FCSTD DOCUMENT  (FreeCAD 0.22R36731 (Git))
Label: bridge_suspend
License: All rights reserved
objects: Part::FeaturePython×17, Part::Extrusion×7, Part::Mirroring×6, Sketcher::SketchObject×5, App::Part×3, Part::Sweep×2, Part::Cut×1, Spreadsheet::Sheet×1, Part::MultiFuse×1
note: 39 computed .brp shape members not serialized (recipe doc carries the construction recipe); baked Part::Feature solids carry a one-line shape summary decoded from their .brp

FEATURE [Part::FeaturePython] HShapeSteel  # WARN: FeaturePython — macro-defined, semantics opaque (R4)
  B = 175
  H = 350
  L = 1000
  Placement = pos=(0,500,0) rot=(0,0,-1;1.5708rad)
  Solid = false
  g0 = 7.85
  mass = 0
  size = 11
  standard = SS_Thin
  t1 = 7
  t2 = 11
FEATURE [Part::FeaturePython] HShapeSteel001  # WARN: FeaturePython — macro-defined, semantics opaque (R4)
  B = 175
  H = 350
  L = 1000
  Placement = pos=(0,-500,0) rot=(0,0,1;1.5708rad)
  Solid = false
  g0 = 7.85
  mass = 0
  size = 11
  standard = SS_Thin
  t1 = 7
  t2 = 11
FEATURE [Part::Extrusion] Extrude
  Base = -> HShapeSteel
  Dir = (1,2e-16,0)
  DirMode = 2
  FaceMakerClass = Part::FaceMakerBullseye
  LengthFwd = 13500
  LengthRev = 0
  Solid = false
  Symmetric = true
  expr: LengthFwd = <<Spreadsheet_bridge>>.tankDia + 500
FEATURE [Part::Extrusion] Extrude001
  Base = -> HShapeSteel001
  Dir = (-1,2e-16,0)
  DirMode = 2
  FaceMakerClass = Part::FaceMakerBullseye
  LengthFwd = 13500
  LengthRev = 0
  Solid = false
  Symmetric = true
  expr: LengthFwd = <<Spreadsheet_bridge>>.tankDia + 500
FEATURE [Sketcher::SketchObject] Sketch
  FullyConstrained = true
  sketch-geometry (5):
    g0: LineSegment StartX=-1000 StartY=-1000 StartZ=0 EndX=1000 EndY=-1000 EndZ=0
    g1: LineSegment StartX=1000 StartY=-1000 StartZ=0 EndX=1000 EndY=1000 EndZ=0
    g2: LineSegment StartX=1000 StartY=1000 StartZ=0 EndX=-1000 EndY=1000 EndZ=0
    g3: LineSegment StartX=-1000 StartY=1000 StartZ=0 EndX=-1000 EndY=-1000 EndZ=0
    g4: GeomPoint X=0 Y=0 Z=0
  constraints (12):
    c: Coincident(g0,g1)
    c: Coincident(g1,g2)
    c: Coincident(g2,g3)
    c: Coincident(g3,g0)
    c: Horizontal(g0)
    c: Horizontal(g2)
    c: Vertical(g1)
    c: Vertical(g3)
    c: Symmetric(g2,g0,g4)
    c: Coincident(g4,g-1)
    c: DistanceX(g2,g2) = 2000
    c: DistanceY(g3,g3) = 2000
FEATURE [Part::FeaturePython] ChannelSteel  # WARN: FeaturePython — macro-defined, semantics opaque (R4)
  B = 75
  H = 150
  L = 1000
  Placement = pos=(925,0,200) rot=(0,0,1;0rad)
  Solid = false
  g0 = 7.85
  mass = 0
  size = 3
  standard = SS
  t1 = 6.5
  t2 = 10
FEATURE [Part::Sweep] Sweep
  Frenet = true
  Sections = -> [ChannelSteel]
  Solid = true
  Spine = -> Sketch [Edge3,Edge2,Edge1,Edge4]
  Transition = 1
FEATURE [Sketcher::SketchObject] Sketch014
  AttachmentSupport = -> [Extrude]
  FullyConstrained = true
  MapMode = 5
  Placement = pos=(0,0,350) rot=(0,0,1;0rad)
  sketch-geometry (5):
    g0: LineSegment StartX=-410 StartY=-410 StartZ=0 EndX=410 EndY=-410 EndZ=0
    g1: LineSegment StartX=410 StartY=-410 StartZ=0 EndX=410 EndY=410 EndZ=0
    g2: LineSegment StartX=410 StartY=410 StartZ=0 EndX=-410 EndY=410 EndZ=0
    g3: LineSegment StartX=-410 StartY=410 StartZ=0 EndX=-410 EndY=-410 EndZ=0
    g4: GeomPoint X=0 Y=0 Z=0
  constraints (12):
    c: Coincident(g0,g1)
    c: Coincident(g1,g2)
    c: Coincident(g2,g3)
    c: Coincident(g3,g0)
    c: Horizontal(g0)
    c: Horizontal(g2)
    c: Vertical(g1)
    c: Vertical(g3)
    c: Symmetric(g2,g0,g4)
    c: Coincident(g4,g-1)
    c: DistanceY(g1,g1) = 820
    c: DistanceX(g2,g2) = 820
FEATURE [Part::Extrusion] Extrude009
  Base = -> Sketch014
  Dir = (0,0,1)
  DirMode = 2
  FaceMakerClass = Part::FaceMakerBullseye
  LengthFwd = 20
  LengthRev = 0
  Solid = true
  Symmetric = false
FEATURE [Part::FeaturePython] ChannelSteel001  # WARN: FeaturePython — macro-defined, semantics opaque (R4)
  B = 75
  H = 150
  L = 1000
  Placement = pos=(315,0,200) rot=(0,0,1;0rad)
  Solid = false
  g0 = 7.85
  mass = 0
  size = 3
  standard = SS
  t1 = 6.5
  t2 = 10
FEATURE [Part::Extrusion] Extrude010
  Base = -> ChannelSteel001
  Dir = (0,1,0)
  DirMode = 2
  FaceMakerClass = Part::FaceMakerBullseye
  LengthFwd = 825
  LengthRev = 0
  Solid = false
  Symmetric = true
FEATURE [Part::FeaturePython] Clone001  label="Extrude011"  # Draft clone (typed FeaturePython)
  AttacherType = Attacher::AttachEngine3D
  Fuse = false
  Objects = -> [Extrude010]
  Placement = pos=(7065,-6.2e-14,0) rot=(0,0,1;3.14159rad)
  Scale = (1,1,1)
  expr: .Placement.Base.x = <<Spreadsheet_bridge>>.tankDia / 2 + 565
FEATURE [Part::FeaturePython] Clone002  label="Extrude012"  # Draft clone (typed FeaturePython)
  AttacherType = Attacher::AttachEngine3D
  Fuse = false
  Objects = -> [Extrude010]
  Placement = pos=(1250,0,0) rot=(0,0,1;0rad)
  Scale = (1,1,1)
FEATURE [Part::FeaturePython] Array006  # Draft array (typed FeaturePython)
  Angle = 360
  ArrayType = 0
  Axis = (0,0,1)
  Base = -> Clone002
  Center = (0,0,0)
  Count = 5
  Fuse = false
  IntervalAxis = (0,0,0)
  IntervalX = (1000,0,0)
  IntervalY = (0,100,0)
  IntervalZ = (0,0,100)
  NumberCircles = 3
  NumberPolar = 5
  NumberX = 5
  NumberY = 1
  NumberZ = 1
  RadialDistance = 50
  Symmetry = 1
  TangentialDistance = 25
FEATURE [Part::Mirroring] Mirror  label="Array006 (mirrored)"
  Base = (0,1200,0)
  Normal = (1,0,0)
  Source = -> Array006
FEATURE [Part::Mirroring] Mirror001  label="Extrude011 (mirrored)"
  Base = (0,1200,0)
  Normal = (1,0,0)
  Source = -> Clone001
FEATURE [Part::Mirroring] Mirror002  label="Extrude010 (mirrored)"
  Base = (0,1200,0)
  Normal = (1,0,0)
  Source = -> Extrude010
FEATURE [Sketcher::SketchObject] Sketch015
  AttachmentSupport = -> [Extrude009]
  FullyConstrained = true
  MapMode = 5
  Placement = pos=(0,0,370) rot=(0,0,1;0rad)
  sketch-geometry (1):
    g0: Circle CenterX=0 CenterY=0 CenterZ=0 NormalX=0 NormalY=0 NormalZ=1 AngleXU=0 Radius=150
  constraints (2):
    c: Coincident(g0,g-1)
    c: Diameter(g0) = 300
FEATURE [Part::Extrusion] Extrude011  label="Extrude013"
  Base = -> Sketch015
  Dir = (0,0,1)
  DirMode = 2
  FaceMakerClass = Part::FaceMakerBullseye
  LengthFwd = -20
  LengthRev = 0
  Solid = true
  Symmetric = false
FEATURE [Part::Cut] Cut006
  Base = -> Extrude009
  Tool = -> Extrude011
FEATURE [Sketcher::SketchObject] Sketch017
  AttachmentSupport = -> [Extrude001]
  ExternalGeometry = -> [Extrude001]
  FullyConstrained = false
  MapMode = 5
  Placement = pos=(0,0,350) rot=(0,0,1;0rad)
  sketch-geometry (3):
    g0: LineSegment StartX=6750 StartY=-412.5 StartZ=0 EndX=6750 EndY=-1000 EndZ=0
    g1: LineSegment StartX=6750 StartY=-1000 StartZ=0 EndX=5250 EndY=-1000 EndZ=0
    g2: LineSegment StartX=5250 StartY=-1000 StartZ=0 EndX=5250 EndY=-412.5 EndZ=0
  constraints (9):
    c: Vertical(g0)
    c: Coincident(g0,g1)
    c: Horizontal(g1)
    c: Coincident(g1,g2)
    c: Vertical(g2)
    c: DistanceX(g1,g1) = 1500
    c: Equal(g2,g0)
    c: Distance(g2,g-1) = 412.5
    c: PointOnObject(g0,g-3)
FEATURE [Part::FeaturePython] ChannelSteel002  # WARN: FeaturePython — macro-defined, semantics opaque (R4)
  B = 75
  H = 150
  L = 1000
  Placement = pos=(6300,-925,200) rot=(0,0,-1;1.5708rad)
  Solid = false
  g0 = 7.85
  mass = 0
  size = 3
  standard = SS
  t1 = 6.5
  t2 = 10
  expr: .Placement.Base.x = <<Spreadsheet_bridge>>.tankDia / 2 - 200
FEATURE [Part::Sweep] Sweep001
  Frenet = true
  Sections = -> [ChannelSteel002]
  Solid = true
  Spine = -> Sketch017 [Edge3,Edge2,Edge1]
  Transition = 1
FEATURE [Sketcher::SketchObject] Sketch016
  AttachmentSupport = -> [Extrude]
  ExternalGeometry = -> [Extrude,Extrude001,Sweep,Cut006,Sweep001]
  FullyConstrained = false
  MapMode = 5
  Placement = pos=(0,0,350) rot=(0,0,1;0rad)
  sketch-geometry (20):
    g0: LineSegment StartX=-6750 StartY=500 StartZ=0 EndX=-1000 EndY=500 EndZ=0
    g1: LineSegment StartX=-1000 StartY=500 StartZ=0 EndX=-1000 EndY=1000 EndZ=0
    g2: LineSegment StartX=-1000 StartY=1000 StartZ=0 EndX=1000 EndY=1000 EndZ=0
    g3: LineSegment StartX=1000 StartY=1000 StartZ=0 EndX=1000 EndY=500 EndZ=0
    g4: LineSegment StartX=1000 StartY=500 StartZ=0 EndX=6750 EndY=500 EndZ=0
    g5: LineSegment StartX=6750 StartY=500 StartZ=0 EndX=6750 EndY=-500 EndZ=0
    g6: LineSegment StartX=5250 StartY=-500 StartZ=0 EndX=1000 EndY=-500 EndZ=0
    g7: LineSegment StartX=1000 StartY=-500 StartZ=0 EndX=1000 EndY=-1000 EndZ=0
    g8: LineSegment StartX=1000 StartY=-1000 StartZ=0 EndX=-1000 EndY=-1000 EndZ=0
    g9: LineSegment StartX=-1000 StartY=-1000 StartZ=0 EndX=-1000 EndY=-500 EndZ=0
    g10: LineSegment StartX=-1000 StartY=-500 StartZ=0 EndX=-6750 EndY=-500 EndZ=0
    g11: LineSegment StartX=-6750 StartY=-500 StartZ=0 EndX=-6750 EndY=500 EndZ=0
    g12: LineSegment StartX=-410 StartY=-410 StartZ=0 EndX=410 EndY=-410 EndZ=0
    g13: LineSegment StartX=410 StartY=-410 StartZ=0 EndX=410 EndY=410 EndZ=0
    g14: LineSegment StartX=410 StartY=410 StartZ=0 EndX=-410 EndY=410 EndZ=0
    g15: LineSegment StartX=-410 StartY=410 StartZ=0 EndX=-410 EndY=-410 EndZ=0
    g16: GeomPoint X=0 Y=0 Z=0
    g17: LineSegment StartX=5250 StartY=-500 StartZ=0 EndX=5250 EndY=-1000 EndZ=0
    g18: LineSegment StartX=5250 StartY=-1000 StartZ=0 EndX=6750 EndY=-1000 EndZ=0
    g19: LineSegment StartX=6750 StartY=-1000 StartZ=0 EndX=6750 EndY=-500 EndZ=0
  constraints (46):
    c: Horizontal(g0)
    c: Coincident(g0,g1)
    c: Coincident(g1,g2)
    c: Coincident(g2,g3)
    c: Vertical(g3)
    c: Coincident(g3,g4)
    c: Horizontal(g4)
    c: Coincident(g4,g5)
    c: Horizontal(g6)
    c: Coincident(g6,g7)
    c: Coincident(g7,g8)
    c: Coincident(g8,g9)
    c: Coincident(g9,g10)
    c: Horizontal(g10)
    c: Coincident(g10,g11)
    c: Coincident(g11,g0)
    c: Coincident(g-3,g0)
    c: Coincident(g10,g-4)
    c: Coincident(g8,g-5)
    c: Vertical(g9)
    c: Vertical(g1)
    c: Coincident(g-6,g1)
    c: Vertical(g7)
    c: Coincident(g7,g-5)
    c: Coincident(g-6,g2)
    c: Coincident(g4,g-7)
    c: Coincident(g5,g-8)
    c: Coincident(g12,g13)
    c: Coincident(g13,g14)
    c: Coincident(g14,g15)
    c: Coincident(g15,g12)
    c: Horizontal(g12)
    c: Horizontal(g14)
    c: Vertical(g13)
    c: Vertical(g15)
    c: Symmetric(g14,g12,g16)
    c: Coincident(g16,g-1)
    c: Coincident(g-9,g13)
    c: Vertical(g17)
    c: Coincident(g17,g18)
    c: Horizontal(g18)
    c: Coincident(g18,g19)
    c: Coincident(g19,g5)
    c: Vertical(g19)
    c: Coincident(g6,g17)
    c: Coincident(g17,g-11)
FEATURE [Part::Extrusion] Extrude012  label="floorPlate"
  Base = -> Sketch016
  Dir = (0,0,1)
  DirMode = 2
  FaceMakerClass = Part::FaceMakerBullseye
  LengthFwd = 4.5
  LengthRev = 0
  Solid = true
  Symmetric = false
FEATURE [Part::FeaturePython] Channel  # WARN: FeaturePython — macro-defined, semantics opaque (R4)
  Placement = pos=(0,-975,354) rot=(0,0,1;0rad)
  Reverse = false
  g0 = 7.85
  h = 1100
  k = 90
  l1 = 975
  l2 = 300
  mass = 23.2452
  p = 500
  spec = 0
  type = 6
FEATURE [Part::FeaturePython] Corner  # WARN: FeaturePython — macro-defined, semantics opaque (R4)
  Placement = pos=(5275,-674,354) rot=(0,0,-1;1.5708rad)
  Reverse = false
  g0 = 7.85
  h = 1100
  k = 90
  l1 = 300
  l2 = 1000
  mass = 13.2836
  p = 1000
  spec = 0
  type = 2
  expr: .Placement.Base.x = <<Spreadsheet_bridge>>.tankDia / 2 - 1225
FEATURE [Part::FeaturePython] Corner_with_end001  # WARN: FeaturePython — macro-defined, semantics opaque (R4)
  Placement = pos=(6725,-474,354) rot=(0,0,-1;1.5708rad)
  Reverse = true
  g0 = 7.85
  h = 1100
  k = -90
  l1 = 500
  l2 = 448
  mass = 14.5547
  p = 500
  spec = 0
  type = 1
  expr: .Placement.Base.x = <<Spreadsheet_bridge>>.tankDia / 2 + 225
FEATURE [Part::Mirroring] Mirror003  label="Channel (mirrored)"
  Base = (-7500,0,0)
  Normal = (0,-1,0)
  Source = -> Channel
FEATURE [Spreadsheet::Sheet] Spreadsheet  label="Spreadsheet_bridge"
  cells = A2='tankDia  Dia; B2(tankDia)=13000
FEATURE [Part::FeaturePython] Corner_with_end  # WARN: FeaturePython — macro-defined, semantics opaque (R4)
  Placement = pos=(-6685,-475,354) rot=(0,0,1;0rad)
  Reverse = false
  g0 = 7.85
  h = 1100
  k = -90
  l1 = 5710
  l2 = 200
  mass = 84.3322
  p = 500
  spec = 0
  type = 1
  expr: .Placement.Base.x = -<<Spreadsheet_bridge>>.tankDia / 2 - 185
  expr: l1 = <<Spreadsheet_bridge>>.tankDia / 2 - 790
FEATURE [Part::FeaturePython] Channel001  # WARN: FeaturePython — macro-defined, semantics opaque (R4)
  Placement = pos=(3125,-473,354) rot=(0,0,1;3.14159rad)
  Reverse = true
  g0 = 7.85
  h = 1100
  k = 90
  l1 = 2150
  l2 = 200
  mass = 49.8434
  p = 1000
  spec = 0
  type = 6
  expr: .Placement.Base.x = <<Spreadsheet_bridge>>.tankDia / 4 - 125
  expr: l1 = (<<Spreadsheet_bridge>>.tankDia / 2 - 2200) / 2
FEATURE [Part::Mirroring] Mirror004  label="Corner_with_end (mirrored)"
  Base = (-9000,0,0)
  Normal = (0,-1,0)
  Source = -> Corner_with_end
FEATURE [Part::Mirroring] Mirror005  label="Corner_with_end (mirrored) (mirrored)"
  Base = (0,1800,0)
  Normal = (1,0,0)
  Source = -> Mirror004
FEATURE [App::Part] Part007  label="handrail"
  Group = -> [Corner,Corner_with_end001,Channel,Mirror003,Corner_with_end,Channel001,Mirror004,Mirror005]
  Origin = -> Origin013
FEATURE [Part::FeaturePython] BasePlate  # WARN: FeaturePython — macro-defined, semantics opaque (R4)
  B = 225
  D = 20
  H = 225
  b1 = 30
  h1 = 65
  sface = 0
FEATURE [Part::FeaturePython] BasePlate001  # WARN: FeaturePython — macro-defined, semantics opaque (R4)
  B = 225
  D = 20
  H = 225
  b1 = 30
  h1 = 65
  sface = 0
FEATURE [Part::Extrusion] Extrude014  label="Extrude015"
  Base = -> BasePlate001
  Dir = (0,0,1)
  DirMode = 2
  FaceMakerClass = Part::FaceMakerBullseye
  LengthFwd = 10
  LengthRev = 0
  Solid = true
  Symmetric = false
FEATURE [Part::FeaturePython] H_Shape001  # WARN: FeaturePython — macro-defined, semantics opaque (R4)
  B = 175
  H = 175
  L = 200
  Solid = true
  g0 = 7.85
  mass = 8.04014
  size = 3
  standard = SS_Wide
FEATURE [Part::MultiFuse] Fusion  label="PostH"
  Placement = pos=(-6662,-412,-200) rot=(0,0,1;4.71239rad)
  Shapes = -> [Extrude014,H_Shape001]
FEATURE [Part::FeaturePython] Array  # Draft array (typed FeaturePython)
  Angle = 360
  ArrayType = 0
  Axis = (0,0,1)
  Base = -> Fusion
  Center = (0,0,0)
  Count = 4
  Fuse = false
  IntervalAxis = (0,0,0)
  IntervalX = (13299.5,0,0)
  IntervalY = (0,825,0)
  IntervalZ = (0,0,100)
  NumberCircles = 3
  NumberPolar = 5
  NumberX = 2
  NumberY = 2
  NumberZ = 1
  RadialDistance = 50
  Symmetry = 1
  TangentialDistance = 25
  expr: .IntervalX.x = <<Spreadsheet_bridge>>.tankDia + 299.5
FEATURE [App::Part] Part006  label="bridgeBody"
  Group = -> [HShapeSteel001,Extrude001,ChannelSteel,Sketch,Sweep,ChannelSteel001,Extrude010,Clone001,Mirror001,Mirror002,Clone002,Array006,Mirror,HShapeSteel,Extrude,Extrude009,Extrude011,Sketch014,Sketch015,Cut006,Sketch016,Extrude012,Sketch017,ChannelSteel002,Sweep001,BasePlate,Extrude014,BasePlate001,H_Shape001,Fusion,Array]
  Origin = -> Origin012
FEATURE [App::Part] Part  label="bridge_suspend"
  Group = -> [Part006,Part007,Spreadsheet]
  Origin = -> Origin
